FREECAD ASSEMBLY — COMPONENT RECIPES ("gripper-assembly")

This assembly document has 31 components, labeled P0..P30 below (a component is one placed body or linked part). 0 of them carry a construction recipe — the FreeCAD feature program that regenerates the part from scratch, quoted from this document or its linked companion documents; the rest are supplied as boundary geometry only. No exploded tour is included for this assembly.
COMPONENT P0 — geometry summary ("Body079 (Mirror #6)"; no construction recipe available for this part):
  bounding box: 68.4 x 38.7 x 6.0 mm
  tessellated surface: 5,294 triangles
  volume: 2788 mm^3 (18% of its bounding box)
COMPONENT P1 — geometry summary ("Body080 (Mirror #7)"; no construction recipe available for this part):
  bounding box: 61.5 x 23.9 x 4.0 mm
  tessellated surface: 4,900 triangles
  volume: 2237 mm^3 (38% of its bounding box)
COMPONENT P2 — geometry summary ("Clone004 (Mirror #5)"; no construction recipe available for this part):
  bounding box: 40.8 x 40.7 x 6.0 mm
  tessellated surface: 3,652 triangles
  volume: 2105 mm^3 (21% of its bounding box)
COMPONENT P3 — geometry summary ("Corps002"; no construction recipe available for this part):
  bounding box: 40.8 x 40.7 x 6.0 mm
  tessellated surface: 3,652 triangles
  volume: 2105 mm^3 (21% of its bounding box)
COMPONENT P4 — geometry summary ("Corps003"; no construction recipe available for this part):
  bounding box: 68.4 x 38.7 x 6.0 mm
  tessellated surface: 5,294 triangles
  volume: 2788 mm^3 (18% of its bounding box)
COMPONENT P5 — geometry summary ("Corps005"; no construction recipe available for this part):
  bounding box: 81.2 x 60.0 x 24.5 mm
  tessellated surface: 10,652 triangles
  volume: 26861 mm^3 (22% of its bounding box)
COMPONENT P6 — geometry summary ("Corps007"; no construction recipe available for this part):
  bounding box: 55.8 x 31.0 x 17.8 mm
  tessellated surface: 3,060 triangles
  volume: 17562 mm^3 (57% of its bounding box)
  symmetry: mirror-symmetric across its x mid-plane
COMPONENT P7 — geometry summary ("Corps008"; no construction recipe available for this part):
  bounding box: 55.8 x 34.1 x 4.0 mm
  tessellated surface: 5,928 triangles
  volume: 3499 mm^3 (46% of its bounding box)
COMPONENT P8 — geometry summary ("Corps010"; no construction recipe available for this part):
  bounding box: 52.0 x 18.8 x 13.9 mm
  tessellated surface: 3,738 triangles
  volume: 6647 mm^3 (49% of its bounding box)
  symmetry: mirror-symmetric across its x mid-plane
COMPONENT P9 — geometry summary ("CorpsRod"; no construction recipe available for this part):
  bounding box: 20.5 x 9.0 x 8.4 mm
  tessellated surface: 7,894 triangles
  volume: 364 mm^3 (23% of its bounding box)
COMPONENT P10 — geometry summary ("CorpsRod001"; no construction recipe available for this part):
  bounding box: 20.5 x 8.9 x 7.8 mm
  tessellated surface: 7,894 triangles
  volume: 364 mm^3 (25% of its bounding box)
COMPONENT P11 — geometry summary ("CorpsRod002"; no construction recipe available for this part):
  bounding box: 20.5 x 9.0 x 8.4 mm
  tessellated surface: 7,894 triangles
  volume: 364 mm^3 (23% of its bounding box)
COMPONENT P12 — geometry summary ("CorpsRod003"; no construction recipe available for this part):
  bounding box: 20.5 x 8.9 x 7.8 mm
  tessellated surface: 7,894 triangles
  volume: 364 mm^3 (25% of its bounding box)
COMPONENT P13 — geometry summary ("ExtensionJawR"; no construction recipe available for this part):
  bounding box: 44.9 x 29.7 x 20.0 mm
  tessellated surface: 4,952 triangles
  volume: 3790 mm^3 (14% of its bounding box)
COMPONENT P14 — geometry summary ("FixationRailServoL"; no construction recipe available for this part):
  bounding box: 25.0 x 23.1 x 20.0 mm
  tessellated surface: 3,014 triangles
  volume: 4036 mm^3 (35% of its bounding box)
COMPONENT P15 — geometry summary ("FixationRailServoR"; no construction recipe available for this part):
  bounding box: 25.0 x 23.1 x 20.0 mm
  tessellated surface: 3,014 triangles
  volume: 4036 mm^3 (35% of its bounding box)
COMPONENT P16 — geometry summary ("JawL"; no construction recipe available for this part):
  bounding box: 99.7 x 84.5 x 79.8 mm
  tessellated surface: 10,624 triangles
  volume: 53122 mm^3 (8% of its bounding box)
COMPONENT P17 — geometry summary ("JawR"; no construction recipe available for this part):
  bounding box: 99.7 x 84.5 x 79.8 mm
  tessellated surface: 10,624 triangles
  volume: 53122 mm^3 (8% of its bounding box)
COMPONENT P18 — geometry summary ("MG996"; no construction recipe available for this part):
  bounding box: 62.7 x 46.0 x 23.5 mm
  tessellated surface: 8,312 triangles
  volume: 32582 mm^3 (48% of its bounding box)
COMPONENT P19 — geometry summary ("MG997"; no construction recipe available for this part):
  bounding box: 62.0 x 46.5 x 36.0 mm
  tessellated surface: 8,312 triangles
  volume: 32582 mm^3 (31% of its bounding box)
COMPONENT P20 — geometry summary ("NoyauRod"; no construction recipe available for this part):
  bounding box: 7.2 x 6.4 x 6.0 mm
  tessellated surface: 5,674 triangles
  volume: 80 mm^3 (29% of its bounding box)
  symmetry: mirror-symmetric across its x mid-plane
COMPONENT P21 — geometry summary ("NoyauRod001"; no construction recipe available for this part):
  bounding box: 7.2 x 6.4 x 6.0 mm
  tessellated surface: 5,674 triangles
  volume: 80 mm^3 (29% of its bounding box)
  symmetry: mirror-symmetric across its x mid-plane
COMPONENT P22 — geometry summary ("NoyauRod002"; no construction recipe available for this part):
  bounding box: 7.2 x 6.4 x 6.0 mm
  tessellated surface: 5,674 triangles
  volume: 80 mm^3 (29% of its bounding box)
  symmetry: 2-fold rotationally symmetric about the x axis; mirror-symmetric across its x mid-plane
COMPONENT P23 — geometry summary ("NoyauRod003"; no construction recipe available for this part):
  bounding box: 7.2 x 6.4 x 6.0 mm
  tessellated surface: 5,674 triangles
  volume: 80 mm^3 (29% of its bounding box)
  symmetry: 2-fold rotationally symmetric about the x axis; mirror-symmetric across its x mid-plane
COMPONENT P24 — geometry summary ("Palonnier"; no construction recipe available for this part):
  bounding box: 61.5 x 23.9 x 4.0 mm
  tessellated surface: 4,018 triangles
  volume: 2268 mm^3 (38% of its bounding box)
COMPONENT P25 — geometry summary ("PalonnierDroit47mm"; no construction recipe available for this part):
  bounding box: 37.5 x 27.9 x 21.6 mm
  tessellated surface: 5,564 triangles
  volume: 1048 mm^3 (5% of its bounding box)
COMPONENT P26 — geometry summary ("Rail MGN9 - 150mm"; no construction recipe available for this part):
  bounding box: 200.0 x 10.6 x 9.6 mm
  tessellated surface: 9,348 triangles
  volume: 9784 mm^3 (48% of its bounding box)
  symmetry: mirror-symmetric across its x mid-plane
COMPONENT P27 — geometry summary ("SupportServoGripper"; no construction recipe available for this part):
  bounding box: 60.0 x 46.3 x 35.2 mm
  tessellated surface: 10,660 triangles
  volume: 14571 mm^3 (15% of its bounding box)
  symmetry: mirror-symmetric across its x mid-plane
COMPONENT P28 — geometry summary ("SupportServoPivot"; no construction recipe available for this part):
  bounding box: 57.6 x 42.8 x 18.5 mm
  tessellated surface: 4,692 triangles
  volume: 13659 mm^3 (30% of its bounding box)
COMPONENT P29 — geometry summary ("mgn9c"; no construction recipe available for this part):
  bounding box: 28.9 x 20.9 x 16.0 mm
  tessellated surface: 4,212 triangles
  volume: 3261 mm^3 (34% of its bounding box)
COMPONENT P30 — geometry summary ("mgn9c001"; no construction recipe available for this part):
  bounding box: 28.9 x 20.9 x 16.0 mm
  tessellated surface: 4,212 triangles
  volume: 3261 mm^3 (34% of its bounding box)
PROVENANCE & LICENSES
A FreeCAD (.FCStd) document from a public repository crawl; recipes are the document's own serialized feature recipes (and, for linked parts, companion documents' recipes).
License: as declared in the source repository (recorded in the dataset sidecar).
